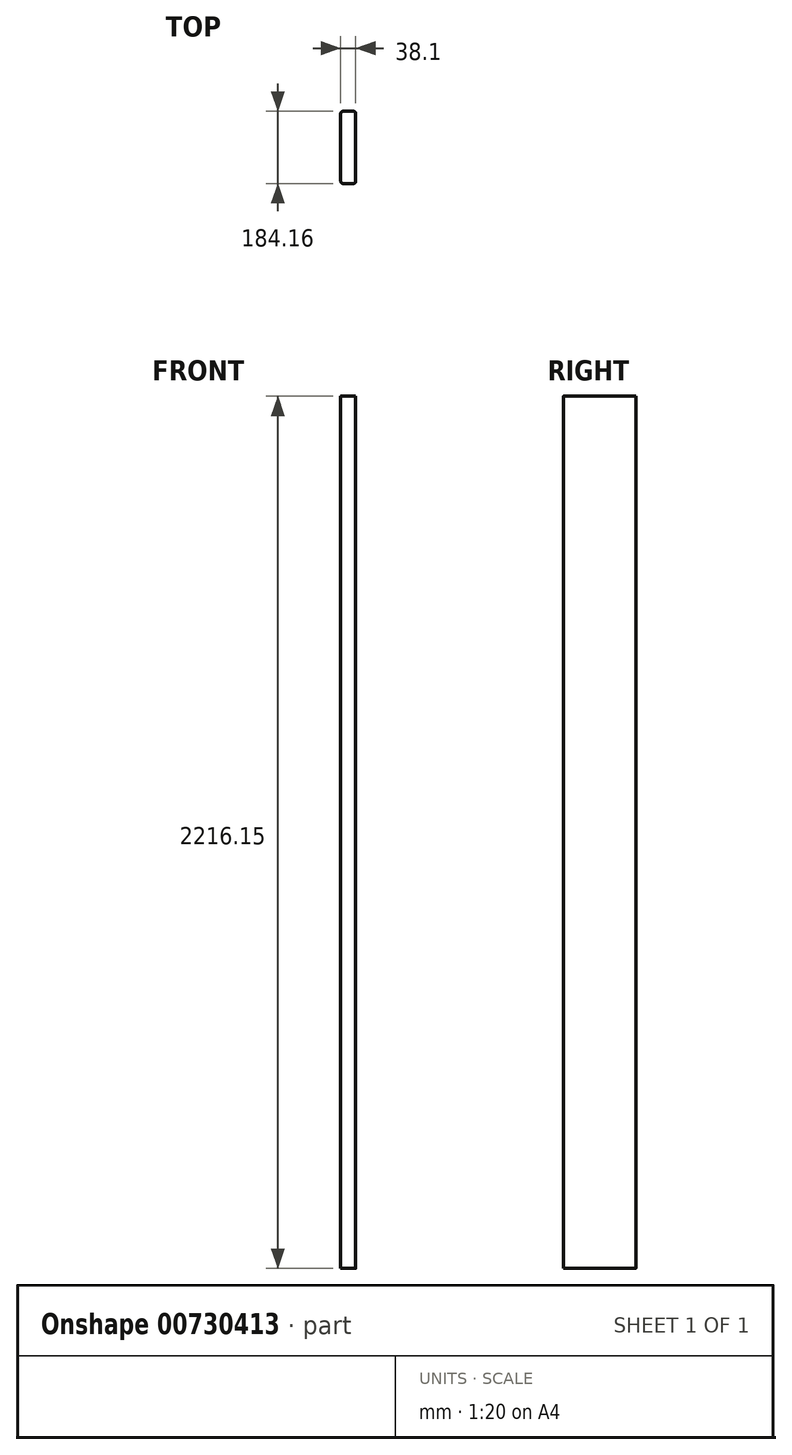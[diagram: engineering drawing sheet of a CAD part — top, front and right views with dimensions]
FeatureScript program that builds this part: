
annotation { "Feature Type Name" : "Feature", "Feature Type Description" : "" }
export const myFeature = defineFeature(function(context is Context, id is Id, definition is map)
    precondition{}
    {
        {
            var Q0;
            Q0=qCreatedBy(makeId("Top.planeOp"),FACE);
            var sketch = newSketch(context, id + "F0", { "sketchPlane" : qUnion([Q0])});
            skLineSegment(sketch, "E0.bottom", {"start": v(-12.7, 92.07) * mm, "end": v(12.7, 92.07) * mm});
            skLineSegment(sketch, "E0.top", {"start": v(-12.7, -92.08) * mm, "end": v(12.7, -92.08) * mm});
            skLineSegment(sketch, "E0.left", {"start": v(-19.05, 85.73) * mm, "end": v(-19.05, -85.73) * mm});
            skLineSegment(sketch, "E0.right", {"start": v(19.05, 85.72) * mm, "end": v(19.05, -85.73) * mm});
            skLineSegment(sketch, "E1", {"start": v(19.05, 92.08) * mm, "end": v(-19.05, -92.08) * mm, "construction": true});
            skPoint(sketch, "E2.visualSharp", {"position": v(-19.05, 92.07) * mm});
            skArc(sketch, "E2.filletArc", {"start": v(-12.7, 92.07) * mm, "mid": v(-17.2, 90.22) * mm, "end": v(-19.05, 85.73) * mm});
            skPoint(sketch, "E3.visualSharp", {"position": v(19.05, 92.08) * mm});
            skArc(sketch, "E3.filletArc", {"start": v(19.05, 85.72) * mm, "mid": v(17.2, 90.22) * mm, "end": v(12.7, 92.07) * mm});
            skPoint(sketch, "E4.visualSharp", {"position": v(19.05, -92.07) * mm});
            skArc(sketch, "E4.filletArc", {"start": v(12.7, -92.08) * mm, "mid": v(17.2, -90.22) * mm, "end": v(19.05, -85.73) * mm});
            skPoint(sketch, "E5.visualSharp", {"position": v(-19.05, -92.08) * mm});
            skArc(sketch, "E5.filletArc", {"start": v(-19.05, -85.73) * mm, "mid": v(-17.2, -90.22) * mm, "end": v(-12.7, -92.08) * mm});
            skSolve(sketch);
        }
        {
            var Q0;
            Q0 = qSketchRegion(id + "F0", true);
            extrude(context, id + "F1", {"entities" : qUnion([Q0]), "depth" : 2216.15 * mm, "offsetDistance" : 25.4 * mm});
        }
    });
